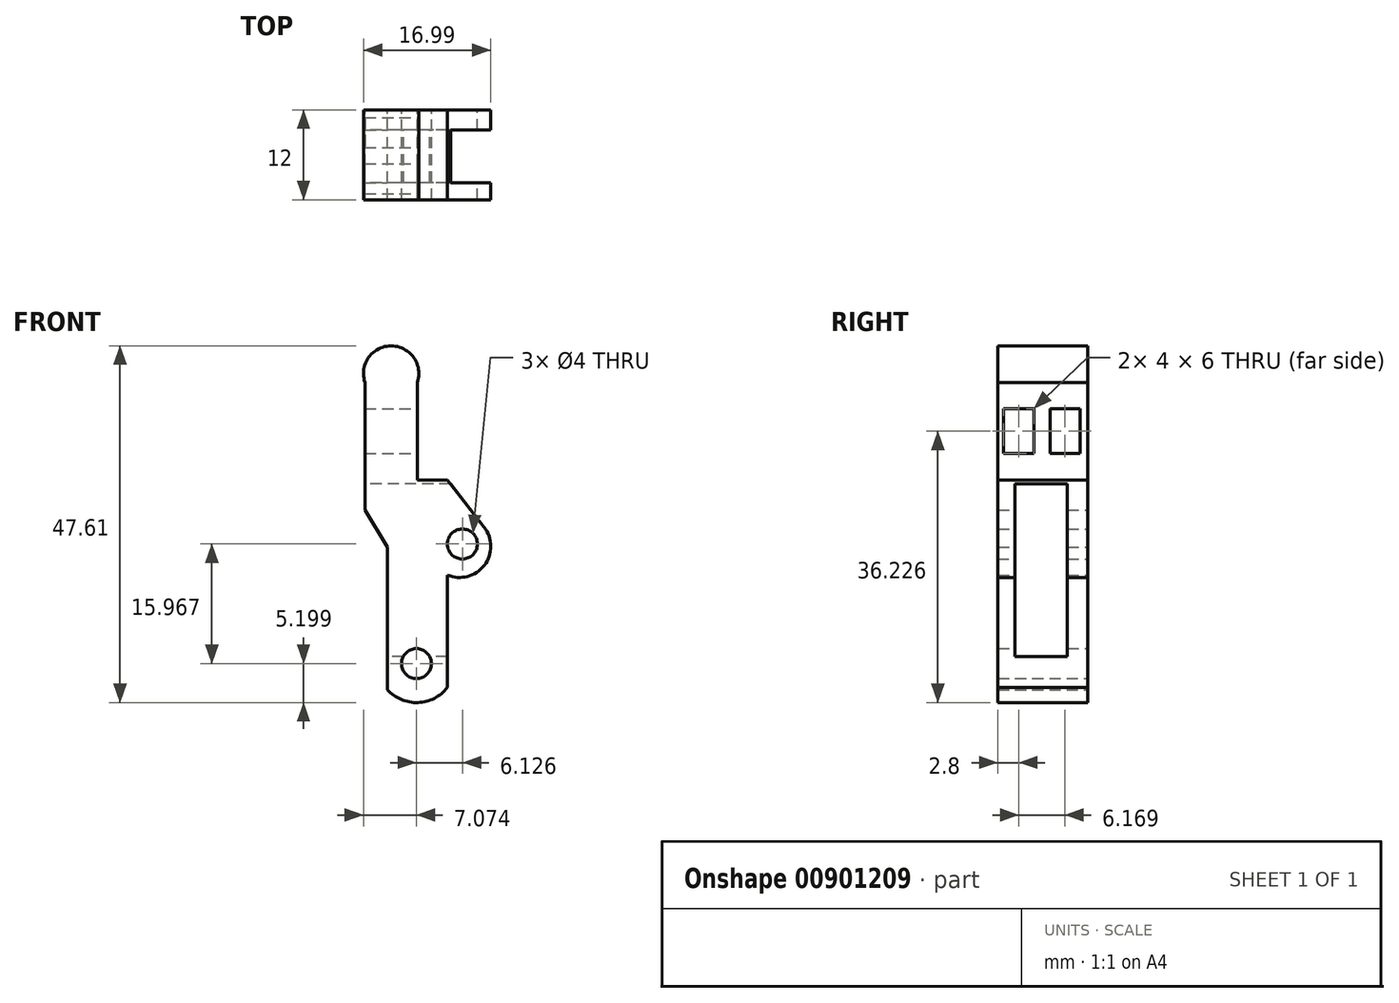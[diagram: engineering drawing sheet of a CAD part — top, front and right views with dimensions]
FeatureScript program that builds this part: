
annotation { "Feature Type Name" : "Feature", "Feature Type Description" : "" }
export const myFeature = defineFeature(function(context is Context, id is Id, definition is map)
    precondition{}
    {
        {
            var Q0;
            Q0=qCreatedBy(makeId("Front.planeOp"),FACE);
            var sketch = newSketch(context, id + "F0", { "sketchPlane" : qUnion([Q0])});
            skLineSegment(sketch, "E0", {"start": v(-3.5, 38.26) * mm, "end": v(-3.5, 21.26) * mm});
            skLineSegment(sketch, "E1", {"start": v(3.5, 38.26) * mm, "end": v(3.5, 25.26) * mm});
            skArc(sketch, "E2", {"start": v(3.5, 38.26) * mm, "mid": v(0, 43.14) * mm, "end": v(-3.5, 38.26) * mm});
            skLineSegment(sketch, "E3", {"start": v(-0.5, 16.26) * mm, "end": v(-0.5, -2.74) * mm});
            skLineSegment(sketch, "E4", {"start": v(-3.5, 21.26) * mm, "end": v(-0.5, 16.26) * mm});
            skLineSegment(sketch, "E5", {"start": v(7.5, 12.56) * mm, "end": v(7.5, -2.44) * mm});
            skArc(sketch, "E6", {"start": v(-0.5, -2.74) * mm, "mid": v(3.57, -4.47) * mm, "end": v(7.5, -2.44) * mm});
            skCircle(sketch, "E7", {"center": v(3.37, 0.73) * mm, "radius": 2 * mm});
            skCircle(sketch, "E8", {"center": v(9.5, 16.7) * mm, "radius": 2 * mm});
            skLineSegment(sketch, "E9", {"start": v(3.5, 25.26) * mm, "end": v(7.5, 25.26) * mm});
            skLineSegment(sketch, "E10", {"start": v(7.5, 25.26) * mm, "end": v(12.41, 18.94) * mm});
            skArc(sketch, "E11", {"start": v(7.5, 12.56) * mm, "mid": v(12.42, 13.85) * mm, "end": v(12.41, 18.94) * mm});
            skSolve(sketch);
        }
        {
            var Q0;
            Q0=makeQuery(id+"F0.imprint","IMPRINT",FACE,{"disambiguationData":[TD([[makeQuery(id+"F0.imprint","IMPRINT",EDGE,{"derivedFrom":sQuery(id+"F0.wireOp",EDGE,"E0")}),1.0]])]});
            extrude(context, id + "F1", {"entities" : qUnion([Q0]), "depth" : 12 * mm, "offsetDistance" : 25 * mm});
        }
        {
            var Q0;
            Q0=makeQuery(id+"F1.opExtrude","SWEPT_FACE",FACE,{"disambiguationData":[OSD([sQuery(id+"F0.wireOp",EDGE,"E1")])]});
            var sketch = newSketch(context, id + "F2", { "sketchPlane" : qUnion([Q0])});
            skLineSegment(sketch, "E12.bottom", {"start": v(-11.2, 34.76) * mm, "end": v(-7.2, 34.76) * mm});
            skLineSegment(sketch, "E12.top", {"start": v(-11.2, 28.76) * mm, "end": v(-7.2, 28.76) * mm});
            skLineSegment(sketch, "E12.left", {"start": v(-11.2, 34.76) * mm, "end": v(-11.2, 28.76) * mm});
            skLineSegment(sketch, "E12.right", {"start": v(-7.2, 34.76) * mm, "end": v(-7.2, 28.76) * mm});
            skLineSegment(sketch, "E13.MirrorCS", {"start": v(-1.03, 28.76) * mm, "end": v(-5.03, 28.76) * mm});
            skLineSegment(sketch, "E14.MirrorCS", {"start": v(-5.03, 34.76) * mm, "end": v(-5.03, 28.76) * mm});
            skLineSegment(sketch, "E15.MirrorCS", {"start": v(-1.03, 34.76) * mm, "end": v(-1.03, 28.76) * mm});
            skLineSegment(sketch, "E16.MirrorCS", {"start": v(-1.03, 34.76) * mm, "end": v(-5.03, 34.76) * mm});
            skSolve(sketch);
        }
        {
            var Q0;
            Q0=makeQuery(id+"F2.imprint","IMPRINT",FACE,{"disambiguationData":[TD([[makeQuery(id+"F2.imprint","IMPRINT",EDGE,{"derivedFrom":sQuery(id+"F2.wireOp",EDGE,"E12.bottom")}),-1.0]])]});
            var Q1;
            Q1=makeQuery(id+"F2.imprint","IMPRINT",FACE,{"disambiguationData":[TD([[makeQuery(id+"F2.imprint","IMPRINT",EDGE,{"derivedFrom":sQuery(id+"F2.wireOp",EDGE,"E13.MirrorCS")}),-1.0]])]});
            extrude(context, id + "F3", {"entities" : qUnion([Q0, Q1]), "operationType" : NewBodyOperationType.REMOVE, "endBound" : BoundingType.THROUGH_ALL, "oppositeDirection" : true, "depth" : 25 * mm, "offsetDistance" : 25 * mm});
        }
        {
            var Q0;
            Q0=qCreatedBy(makeId("Right.planeOp"),FACE);
            var sketch = newSketch(context, id + "F4", { "sketchPlane" : qUnion([Q0])});
            skLineSegment(sketch, "E17.bottom", {"start": v(-2.7, 1.7) * mm, "end": v(-9.7, 1.7) * mm});
            skLineSegment(sketch, "E17.top", {"start": v(-2.7, 24.7) * mm, "end": v(-9.7, 24.7) * mm});
            skLineSegment(sketch, "E17.left", {"start": v(-2.7, 1.7) * mm, "end": v(-2.7, 24.7) * mm});
            skLineSegment(sketch, "E17.right", {"start": v(-9.7, 1.7) * mm, "end": v(-9.7, 24.7) * mm});
            skSolve(sketch);
        }
        {
            var Q0;
            Q0=makeQuery(id+"F4.imprint","IMPRINT",FACE,{"disambiguationData":[TD([[makeQuery(id+"F4.imprint","IMPRINT",EDGE,{"derivedFrom":sQuery(id+"F4.wireOp",EDGE,"E17.bottom")}),-1.0]])]});
            extrude(context, id + "F5", {"entities" : qUnion([Q0]), "operationType" : NewBodyOperationType.REMOVE, "endBound" : BoundingType.THROUGH_ALL, "depth" : 25 * mm, "offsetDistance" : 25 * mm, "hasSecondDirection" : true, "secondDirectionOppositeDirection" : true, "secondDirectionDepth" : 25 * mm});
        }
    });
